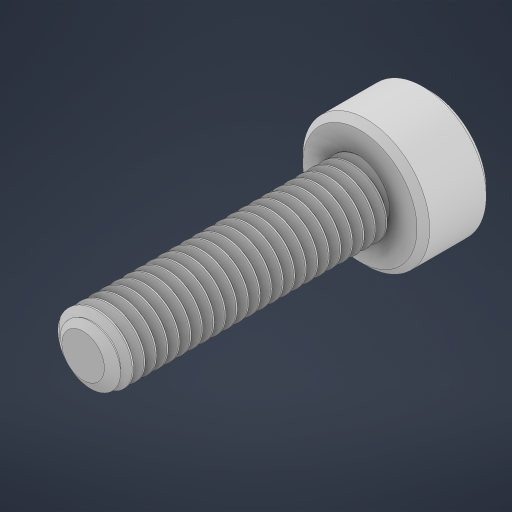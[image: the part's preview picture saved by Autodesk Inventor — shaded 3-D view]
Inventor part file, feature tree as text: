
AUTODESK INVENTOR PART (.ipt)
format: ipt  version: 2023 (Build 270158000, 158)  size: 867,328 bytes
history: native  units: in
note: dims shown in document units (in); Inventor stores cm internally (conversion verified against a paired STEP export)
features: chamfer x1
ambient origin geometry x8: Origin, YZ Plane, XZ Plane, XY Plane, X Axis, Y Axis, Z Axis, Center Point
bodies: Solid1 (feature_tree)
feature tree (1):
  chamfer  "Chamfer1"  [1 undecoded]
note: 1 required parameter value undecoded (feature->parameter linkage not recoverable at this tier; creation-order binding heuristic only, values carry confidence <= 0.55)
